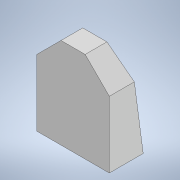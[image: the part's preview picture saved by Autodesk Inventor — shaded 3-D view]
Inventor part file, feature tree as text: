
AUTODESK INVENTOR PART (.ipt)
format: ipt  version: 2021 (Build 250183000, 183)  size: 108,544 bytes
history: native  units: in
note: dims shown in document units (in); Inventor stores cm internally (conversion verified against a paired STEP export)
features: extrude x2, sketch x1
ambient origin geometry x8: Origin, YZ Plane, XZ Plane, XY Plane, X Axis, Y Axis, Z Axis, Center Point
bodies: Solid1 (feature_tree)
feature tree (3):
  extrude  "Extrusion1"  Depth=0.2362in
  extrude  "Extrusion2"  Depth=0.2362in
  sketch  "Sketch1"  dims[d0=0.2362in d1=0.4331in d2=0.2362in d3=0.4331in d4=0.5906in d5=0.0787in d6=0.0787in d7=0.2362in d8=0.0in d9=0.0787in d10=0.7062in d11=0.0in]
